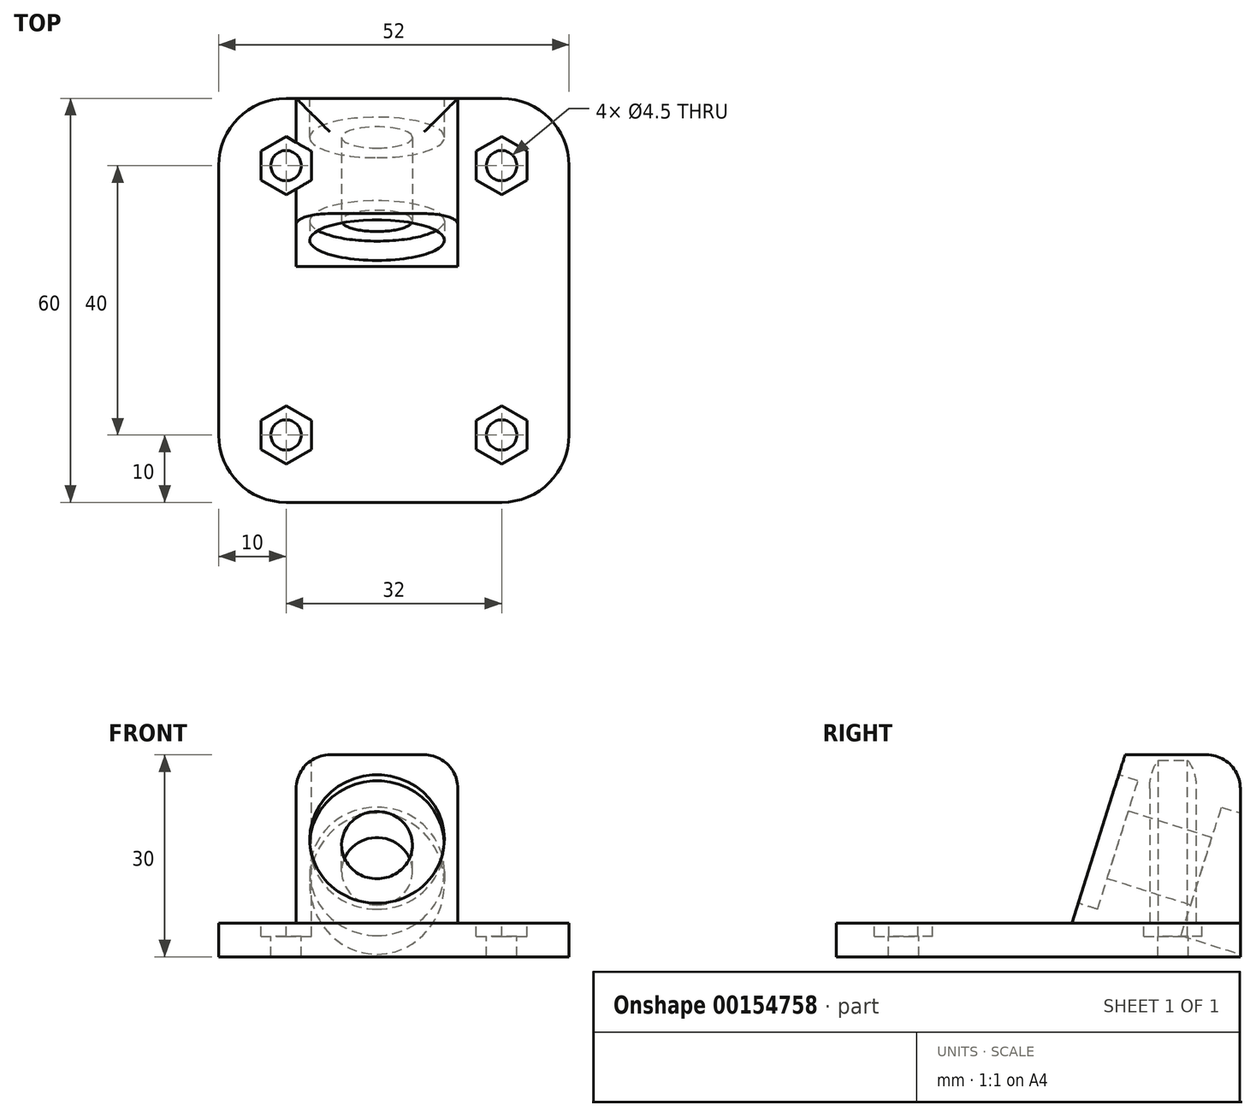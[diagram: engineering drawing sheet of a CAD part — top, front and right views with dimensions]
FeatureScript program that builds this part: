
annotation { "Feature Type Name" : "Feature", "Feature Type Description" : "" }
export const myFeature = defineFeature(function(context is Context, id is Id, definition is map)
    precondition{}
    {
        {
            var Q0;
            Q0=qCreatedBy(makeId("Top.planeOp"),FACE);
            var sketch = newSketch(context, id + "F0", { "sketchPlane" : qUnion([Q0])});
            skLineSegment(sketch, "E0.bottom", {"start": v(26, -30) * mm, "end": v(-26, -30) * mm});
            skLineSegment(sketch, "E0.top", {"start": v(26, 30) * mm, "end": v(-26, 30) * mm});
            skLineSegment(sketch, "E0.left", {"start": v(26, -30) * mm, "end": v(26, 30) * mm});
            skLineSegment(sketch, "E0.right", {"start": v(-26, -30) * mm, "end": v(-26, 30) * mm});
            skPoint(sketch, "E0.middle", {"position": v(0, 0) * mm});
            skSolve(sketch);
        }
        {
            var Q0;
            Q0=qSketchRegion(id+"F0",true);
            extrude(context, id + "F1", {"entities" : qUnion([Q0]), "depth" : 5 * mm});
        }
        {
            var Q0;
            Q0=makeQuery(id+"F1.opExtrude","SWEPT_EDGE",EDGE,{"disambiguationData":[OSD([sQuery(id+"F0.wireOp",EDGE,"E0.bottom"),sQuery(id+"F0.wireOp",EDGE,"E0.left")])]});
            var Q1;
            Q1=makeQuery(id+"F1.opExtrude","SWEPT_EDGE",EDGE,{"disambiguationData":[OSD([sQuery(id+"F0.wireOp",EDGE,"E0.bottom"),sQuery(id+"F0.wireOp",EDGE,"E0.right")])]});
            var Q2;
            Q2=makeQuery(id+"F1.opExtrude","SWEPT_EDGE",EDGE,{"disambiguationData":[OSD([sQuery(id+"F0.wireOp",EDGE,"E0.top"),sQuery(id+"F0.wireOp",EDGE,"E0.left")])]});
            var Q3;
            Q3=makeQuery(id+"F1.opExtrude","SWEPT_EDGE",EDGE,{"disambiguationData":[OSD([sQuery(id+"F0.wireOp",EDGE,"E0.top"),sQuery(id+"F0.wireOp",EDGE,"E0.right")])]});
            fillet(context, id + "F2", {"entities" : qUnion([Q0, Q1, Q2, Q3]), "radius" : 10 * mm, "tangentPropagation" : true, "allowEdgeOverflow" : false});
        }
        {
            var Q0;
            Q0=makeQuery(id+"F1.opExtrude","CAP_FACE",FACE,{"disambiguationData":[OSD([sQuery(id+"F0.wireOp",EDGE,"E0.bottom"),sQuery(id+"F0.wireOp",EDGE,"E0.top"),sQuery(id+"F0.wireOp",EDGE,"E0.left"),sQuery(id+"F0.wireOp",EDGE,"E0.right")])],"isStart":false});
            var sketch = newSketch(context, id + "F3", { "sketchPlane" : qUnion([Q0])});
            skCircle(sketch, "E1", {"center": v(16, -20) * mm, "radius": 2.25 * mm});
            skCircle(sketch, "E2.0.1.0", {"center": v(16, 20) * mm, "radius": 2.25 * mm});
            skCircle(sketch, "E2.1.0.0", {"center": v(-16, -20) * mm, "radius": 2.25 * mm});
            skCircle(sketch, "E2.1.1.0", {"center": v(-16, 20) * mm, "radius": 2.25 * mm});
            skLineSegment(sketch, "E2.direction1", {"start": v(16, -20) * mm, "end": v(-16, -20) * mm, "construction": true});
            skLineSegment(sketch, "E2.direction2", {"start": v(16, -20) * mm, "end": v(16, 20) * mm, "construction": true});
            skSolve(sketch);
        }
        {
            var Q0;
            Q0=makeQuery(id+"F3.imprint","IMPRINT",FACE,{"disambiguationData":[TD([[makeQuery(id+"F3.imprint","IMPRINT",EDGE,{"derivedFrom":sQuery(id+"F3.wireOp",EDGE,"E2.1.0.0")}),1.0]])]});
            var Q1;
            Q1=makeQuery(id+"F3.imprint","IMPRINT",FACE,{"disambiguationData":[TD([[makeQuery(id+"F3.imprint","IMPRINT",EDGE,{"derivedFrom":sQuery(id+"F3.wireOp",EDGE,"E1")}),1.0]])]});
            var Q2;
            Q2=makeQuery(id+"F3.imprint","IMPRINT",FACE,{"disambiguationData":[TD([[makeQuery(id+"F3.imprint","IMPRINT",EDGE,{"derivedFrom":sQuery(id+"F3.wireOp",EDGE,"E2.1.1.0")}),1.0]])]});
            var Q3;
            Q3=makeQuery(id+"F3.imprint","IMPRINT",FACE,{"disambiguationData":[TD([[makeQuery(id+"F3.imprint","IMPRINT",EDGE,{"derivedFrom":sQuery(id+"F3.wireOp",EDGE,"E2.0.1.0")}),1.0]])]});
            extrude(context, id + "F4", {"entities" : qUnion([Q0, Q1, Q2, Q3]), "operationType" : NewBodyOperationType.REMOVE, "oppositeDirection" : true, "depth" : 25 * mm});
        }
        {
            var Q0;
            Q0=makeQuery(id+"F1.opExtrude","CAP_FACE",FACE,{"disambiguationData":[OSD([sQuery(id+"F0.wireOp",EDGE,"E0.bottom"),sQuery(id+"F0.wireOp",EDGE,"E0.top"),sQuery(id+"F0.wireOp",EDGE,"E0.left"),sQuery(id+"F0.wireOp",EDGE,"E0.right")])],"isStart":false});
            var sketch = newSketch(context, id + "F5", { "sketchPlane" : qUnion([Q0])});
            skCircle(sketch, "E3.cCircle", {"center": v(-16, -20) * mm, "radius": 3.75 * mm, "construction": true});
            skLineSegment(sketch, "E3.0", {"start": v(-19.75, -17.83) * mm, "end": v(-16, -15.67) * mm});
            skLineSegment(sketch, "E3.1", {"start": v(-16, -15.67) * mm, "end": v(-12.25, -17.83) * mm});
            skLineSegment(sketch, "E3.2", {"start": v(-12.25, -17.83) * mm, "end": v(-12.25, -22.17) * mm});
            skLineSegment(sketch, "E3.3", {"start": v(-12.25, -22.17) * mm, "end": v(-16, -24.33) * mm});
            skLineSegment(sketch, "E3.4", {"start": v(-16, -24.33) * mm, "end": v(-19.75, -22.17) * mm});
            skLineSegment(sketch, "E3.5", {"start": v(-19.75, -22.17) * mm, "end": v(-19.75, -17.83) * mm});
            skPoint(sketch, "E3.0.midPoint", {"position": v(-17.88, -16.75) * mm});
            skLineSegment(sketch, "E4.0.1.0", {"start": v(-16, 24.33) * mm, "end": v(-12.25, 22.17) * mm});
            skLineSegment(sketch, "E4.0.1.1", {"start": v(-12.25, 22.17) * mm, "end": v(-12.25, 17.83) * mm});
            skLineSegment(sketch, "E4.0.1.2", {"start": v(-12.25, 17.83) * mm, "end": v(-16, 15.67) * mm});
            skLineSegment(sketch, "E4.0.1.3", {"start": v(-16, 15.67) * mm, "end": v(-19.75, 17.83) * mm});
            skLineSegment(sketch, "E4.0.1.4", {"start": v(-19.75, 17.83) * mm, "end": v(-19.75, 22.17) * mm});
            skLineSegment(sketch, "E4.0.1.5", {"start": v(-19.75, 22.17) * mm, "end": v(-16, 24.33) * mm});
            skLineSegment(sketch, "E4.1.0.0", {"start": v(16, -15.67) * mm, "end": v(19.75, -17.83) * mm});
            skLineSegment(sketch, "E4.1.0.1", {"start": v(19.75, -17.83) * mm, "end": v(19.75, -22.17) * mm});
            skLineSegment(sketch, "E4.1.0.2", {"start": v(19.75, -22.17) * mm, "end": v(16, -24.33) * mm});
            skLineSegment(sketch, "E4.1.0.3", {"start": v(16, -24.33) * mm, "end": v(12.25, -22.17) * mm});
            skLineSegment(sketch, "E4.1.0.4", {"start": v(12.25, -22.17) * mm, "end": v(12.25, -17.83) * mm});
            skLineSegment(sketch, "E4.1.0.5", {"start": v(12.25, -17.83) * mm, "end": v(16, -15.67) * mm});
            skLineSegment(sketch, "E4.1.1.0", {"start": v(16, 24.33) * mm, "end": v(19.75, 22.17) * mm});
            skLineSegment(sketch, "E4.1.1.1", {"start": v(19.75, 22.17) * mm, "end": v(19.75, 17.83) * mm});
            skLineSegment(sketch, "E4.1.1.2", {"start": v(19.75, 17.83) * mm, "end": v(16, 15.67) * mm});
            skLineSegment(sketch, "E4.1.1.3", {"start": v(16, 15.67) * mm, "end": v(12.25, 17.83) * mm});
            skLineSegment(sketch, "E4.1.1.4", {"start": v(12.25, 17.83) * mm, "end": v(12.25, 22.17) * mm});
            skLineSegment(sketch, "E4.1.1.5", {"start": v(12.25, 22.17) * mm, "end": v(16, 24.33) * mm});
            skLineSegment(sketch, "E4.direction1", {"start": v(-16, -15.96) * mm, "end": v(16, -15.96) * mm, "construction": true});
            skLineSegment(sketch, "E4.direction2", {"start": v(-16, -15.96) * mm, "end": v(-16, 24.04) * mm, "construction": true});
            skSolve(sketch);
        }
        {
            var Q0;
            Q0=qSketchRegion(id+"F5",true);
            extrude(context, id + "F6", {"entities" : qUnion([Q0]), "operationType" : NewBodyOperationType.REMOVE, "oppositeDirection" : true, "depth" : 2 * mm});
        }
        {
            var Q0;
            Q0=makeQuery(id+"F1.opExtrude","CAP_FACE",FACE,{"disambiguationData":[OSD([sQuery(id+"F0.wireOp",EDGE,"E0.bottom"),sQuery(id+"F0.wireOp",EDGE,"E0.top"),sQuery(id+"F0.wireOp",EDGE,"E0.left"),sQuery(id+"F0.wireOp",EDGE,"E0.right")])],"isStart":false});
            var sketch = newSketch(context, id + "F7", { "sketchPlane" : qUnion([Q0])});
            skLineSegment(sketch, "E5.bottom", {"start": v(9.5, 30) * mm, "end": v(-14.5, 30) * mm});
            skLineSegment(sketch, "E5.top", {"start": v(9.5, 5) * mm, "end": v(-14.5, 5) * mm});
            skLineSegment(sketch, "E5.left", {"start": v(9.5, 30) * mm, "end": v(9.5, 5) * mm});
            skLineSegment(sketch, "E5.right", {"start": v(-14.5, 30) * mm, "end": v(-14.5, 5) * mm});
            skPoint(sketch, "E5.middle", {"position": v(-2.5, 17.5) * mm});
            skSolve(sketch);
        }
        {
            var Q0;
            Q0=qSketchRegion(id+"F7",true);
            extrude(context, id + "F8", {"entities" : qUnion([Q0]), "operationType" : NewBodyOperationType.ADD, "depth" : 25 * mm});
        }
        {
            var Q0;
            Q0=makeQuery(id+"F8.opExtrude","SWEPT_FACE",FACE,{"disambiguationData":[OSD([sQuery(id+"F7.wireOp",EDGE,"E5.right")])]});
            var sketch = newSketch(context, id + "F9", { "sketchPlane" : qUnion([Q0])});
            skLineSegment(sketch, "E6", {"start": v(-5, 5) * mm, "end": v(-12.88, 30) * mm});
            skLineSegment(sketch, "E7", {"start": v(-12.88, 30) * mm, "end": v(-5, 30) * mm});
            skLineSegment(sketch, "E8", {"start": v(-5, 30) * mm, "end": v(-5, 5) * mm});
            skSolve(sketch);
        }
        {
            var Q0;
            Q0=makeQuery(id+"F9.imprint","IMPRINT",FACE,{"disambiguationData":[TD([[makeQuery(id+"F9.imprint","IMPRINT",EDGE,{"derivedFrom":sQuery(id+"F9.wireOp",EDGE,"E6")}),-1.0]])]});
            extrude(context, id + "F10", {"entities" : qUnion([Q0]), "operationType" : NewBodyOperationType.REMOVE, "endBound" : BoundingType.THROUGH_ALL, "oppositeDirection" : true, "depth" : 25 * mm});
        }
        {
            var Q0;
            Q0=makeQuery(id+"F10.boolean.opBoolean","COPY",FACE,{"derivedFrom":makeQuery(id+"F10.opExtrude","SWEPT_FACE",FACE,{"disambiguationData":[OSD([sQuery(id+"F9.wireOp",EDGE,"E6")])]})});
            var sketch = newSketch(context, id + "F11", { "sketchPlane" : qUnion([Q0])});
            skLineSegment(sketch, "E9", {"start": v(-14.5, 6.27) * mm, "end": v(-14.5, 32.49) * mm});
            skLineSegment(sketch, "E10", {"start": v(-14.5, 32.49) * mm, "end": v(9.5, 32.49) * mm});
            skLineSegment(sketch, "E11", {"start": v(9.5, 32.49) * mm, "end": v(9.5, 6.27) * mm});
            skLineSegment(sketch, "E12", {"start": v(9.5, 6.27) * mm, "end": v(-14.5, 6.27) * mm});
            skCircle(sketch, "E13", {"center": v(-2.5, 19.38) * mm, "radius": 5.25 * mm});
            skPoint(sketch, "E13.centerSnap0", {"position": v(-2.5, 32.49) * mm});
            skPoint(sketch, "E13.centerSnap1", {"position": v(-14.5, 19.38) * mm});
            skSolve(sketch);
        }
        {
            var Q0;
            Q0=makeQuery(id+"F11.imprint","IMPRINT",FACE,{"disambiguationData":[TD([[makeQuery(id+"F11.imprint","IMPRINT",EDGE,{"derivedFrom":sQuery(id+"F11.wireOp",EDGE,"E13")}),1.0]])]});
            extrude(context, id + "F12", {"entities" : qUnion([Q0]), "operationType" : NewBodyOperationType.REMOVE, "endBound" : BoundingType.THROUGH_ALL, "oppositeDirection" : true, "depth" : 25 * mm});
        }
        {
            var Q0;
            Q0=makeQuery(id+"F10.boolean.opBoolean","COPY",FACE,{"derivedFrom":makeQuery(id+"F10.opExtrude","SWEPT_FACE",FACE,{"disambiguationData":[OSD([sQuery(id+"F9.wireOp",EDGE,"E6")])]})});
            var sketch = newSketch(context, id + "F13", { "sketchPlane" : qUnion([Q0])});
            skCircle(sketch, "E14", {"center": v(-2.5, 19.38) * mm, "radius": 10 * mm});
            skSolve(sketch);
        }
        {
            var Q0;
            Q0=makeQuery(id+"F13.imprint","IMPRINT",FACE,{"disambiguationData":[TD([[makeQuery(id+"F13.imprint","IMPRINT",EDGE,{"derivedFrom":sQuery(id+"F13.wireOp",EDGE,"E14")}),1.0]])]});
            extrude(context, id + "F14", {"entities" : qUnion([Q0]), "operationType" : NewBodyOperationType.REMOVE, "oppositeDirection" : true, "depth" : 3 * mm});
        }
        {
            var Q0;
            Q0=makeQuery(id+"F10.boolean.opBoolean","COPY",FACE,{"derivedFrom":makeQuery(id+"F10.opExtrude","SWEPT_FACE",FACE,{"disambiguationData":[OSD([sQuery(id+"F9.wireOp",EDGE,"E6")])]})});
            cPlane(context, id + "F15", {"entities" : qUnion([Q0]), "cplaneType" : CPlaneType.OFFSET, "offset" : 28 * mm, "oppositeDirection" : true, "width" : 150 * mm, "height" : 150 * mm});
        }
        {
            var Q0;
            Q0=qCreatedBy(id+"F15.planeOp",FACE);
            var sketch = newSketch(context, id + "F16", { "sketchPlane" : qUnion([Q0])});
            skCircle(sketch, "E15", {"center": v(-2.5, 19.38) * mm, "radius": 10 * mm});
            skSolve(sketch);
        }
        {
            var Q0;
            Q0 = qSketchRegion(id + "F16", true);
            extrude(context, id + "F17", {"entities" : qUnion([Q0]), "operationType" : NewBodyOperationType.REMOVE, "depth" : 12 * mm});
        }
        {
            var Q0;
            Q0 = qSketchRegion(id + "F5", true);
            extrude(context, id + "F18", {"entities" : qUnion([Q0]), "operationType" : NewBodyOperationType.REMOVE, "endBound" : BoundingType.THROUGH_ALL, "depth" : 25 * mm});
        }
        {
            var Q0;
            {var subQ0=sQuery(id+"F7.wireOp",EDGE,"E5.right");Q0=makeQuery(id+"F18.boolean.opBoolean","SPLIT",EDGE,{"disambiguationData":[TD([makeQuery(id+"F1.opExtrude","SWEPT_FACE",FACE,{"disambiguationData":[OSD([sQuery(id+"F0.wireOp",EDGE,"E0.top")])]})])],"derivedFrom":makeQuery(id+"F8.opExtrude","CAP_EDGE",EDGE,{"disambiguationData":[OSD([subQ0])],"isStart":false})});}
            var Q1;
            {var subQ0=sQuery(id+"F7.wireOp",EDGE,"E5.right");var subQ1=sQuery(id+"F5.wireOp",EDGE,"E4.0.1.2");Q1=makeQuery(id+"F18.boolean.opBoolean","SPLIT",EDGE,{"disambiguationData":[TD([makeQuery(id+"F6.boolean.opBoolean","COPY",FACE,{"derivedFrom":makeQuery(id+"F6.opExtrude","SWEPT_FACE",FACE,{"disambiguationData":[OSD([subQ1])]})})])],"derivedFrom":makeQuery(id+"F8.opExtrude","CAP_EDGE",EDGE,{"disambiguationData":[OSD([subQ0])],"isStart":false})});}
            var Q2;
            Q2=makeQuery(id+"F8.opExtrude","CAP_EDGE",EDGE,{"disambiguationData":[OSD([sQuery(id+"F7.wireOp",EDGE,"E5.left")])],"isStart":false});
            var Q3;
            Q3=makeQuery(id+"F8.opExtrude","CAP_EDGE",EDGE,{"disambiguationData":[OSD([sQuery(id+"F7.wireOp",EDGE,"E5.bottom")])],"isStart":false});
            var Q4;
            Q4=makeQuery(id+"F10.boolean.opBoolean","MERGE",EDGE,{"derivedFrom":[makeQuery(id+"F8.opExtrude","CAP_EDGE",EDGE,{"disambiguationData":[OSD([sQuery(id+"F7.wireOp",EDGE,"E5.top")])],"isStart":true}),makeQuery(id+"F10.opExtrude","SWEPT_EDGE",EDGE,{"disambiguationData":[OSD([sQuery(id+"F7.wireOp",EDGE,"E5.right"),sQuery(id+"F9.wireOp",EDGE,"E6"),sQuery(id+"F9.wireOp",EDGE,"E8")])]})]});
            fillet(context, id + "F19", {"entities" : qUnion([Q0, Q1, Q2, Q3, Q4]), "radius" : 5 * mm, "tangentPropagation" : true, "allowEdgeOverflow" : false});
        }
    });
